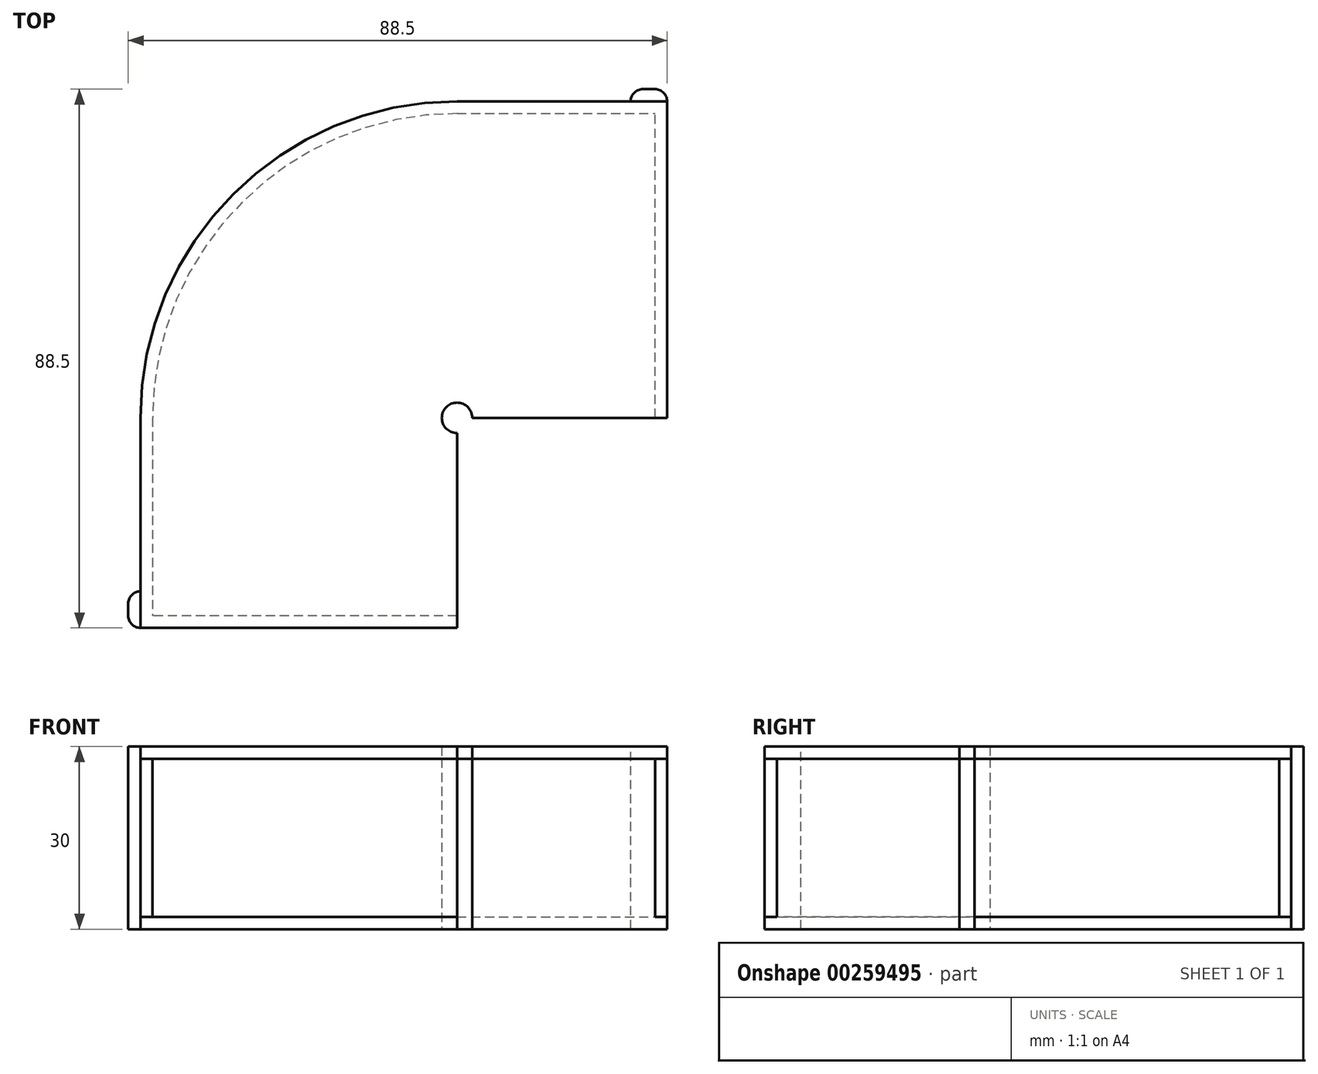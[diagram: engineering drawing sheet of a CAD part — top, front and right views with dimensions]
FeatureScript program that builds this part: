
annotation { "Feature Type Name" : "Feature", "Feature Type Description" : "" }
export const myFeature = defineFeature(function(context is Context, id is Id, definition is map)
    precondition{}
    {
        {
            var Q0;
            Q0=qCreatedBy(makeId("Top.planeOp"),FACE);
            var sketch = newSketch(context, id + "F0", { "sketchPlane" : qUnion([Q0])});
            skLineSegment(sketch, "E0.bottom", {"start": v(2.5, 0) * mm, "end": v(32.5, 0) * mm});
            skLineSegment(sketch, "E0.left", {"start": v(0, -2.5) * mm, "end": v(0, -32.5) * mm});
            skLineSegment(sketch, "E1.0", {"start": v(0, 50) * mm, "end": v(32.5, 50) * mm});
            skLineSegment(sketch, "E1.1", {"start": v(-50, 0) * mm, "end": v(-50, -32.5) * mm});
            skLineSegment(sketch, "E2", {"start": v(0, -32.5) * mm, "end": v(-50, -32.5) * mm});
            skLineSegment(sketch, "E3", {"start": v(32.5, 0) * mm, "end": v(32.5, 50) * mm});
            skArc(sketch, "E4", {"start": v(2.5, 0) * mm, "mid": v(-1.77, 1.77) * mm, "end": v(0, -2.5) * mm});
            skPoint(sketch, "E5.visualSharp", {"position": v(-50, 50) * mm});
            skArc(sketch, "E5.filletArc", {"start": v(0, 50) * mm, "mid": v(-35.36, 35.36) * mm, "end": v(-50, 0) * mm});
            skSolve(sketch);
        }
        {
            var Q0;
            Q0=makeQuery(id+"F0.imprint","IMPRINT",FACE,{"disambiguationData":[TD([[makeQuery(id+"F0.imprint","IMPRINT",EDGE,{"derivedFrom":sQuery(id+"F0.wireOp",EDGE,"E0.bottom")}),1.0]])]});
            extrude(context, id + "F1", {"entities" : qUnion([Q0]), "depth" : 26 * mm});
        }
        {
            var Q0;
            Q0=makeQuery(id+"F1.opExtrude","CAP_FACE",FACE,{"disambiguationData":[OSD([sQuery(id+"F0.wireOp",EDGE,"E0.bottom"),sQuery(id+"F0.wireOp",EDGE,"E0.left"),sQuery(id+"F0.wireOp",EDGE,"E1.0"),sQuery(id+"F0.wireOp",EDGE,"E1.1"),sQuery(id+"F0.wireOp",EDGE,"E2"),sQuery(id+"F0.wireOp",EDGE,"E3"),sQuery(id+"F0.wireOp",EDGE,"E4"),sQuery(id+"F0.wireOp",EDGE,"E5.filletArc")])],"isStart":false});
            var sketch = newSketch(context, id + "F2", { "sketchPlane" : qUnion([Q0])});
            skLineSegment(sketch, "E6.0", {"start": v(34.5, 52) * mm, "end": v(0, 52) * mm});
            skLineSegment(sketch, "E6.1", {"start": v(34.5, 0) * mm, "end": v(34.5, 52) * mm});
            skLineSegment(sketch, "E6.2", {"start": v(-52, 0) * mm, "end": v(-52, -34.5) * mm});
            skLineSegment(sketch, "E6.3", {"start": v(-52, -34.5) * mm, "end": v(0, -34.5) * mm});
            skArc(sketch, "E6.5", {"start": v(0, 52) * mm, "mid": v(-36.77, 36.77) * mm, "end": v(-52, 0) * mm});
            skLineSegment(sketch, "E7.0", {"start": v(2.5, 0) * mm, "end": v(34.5, 0) * mm});
            skArc(sketch, "E8.0", {"start": v(2.5, 0) * mm, "mid": v(-1.77, 1.77) * mm, "end": v(0, -2.5) * mm});
            skLineSegment(sketch, "E9.0", {"start": v(0, -2.5) * mm, "end": v(0, -34.5) * mm});
            skPoint(sketch, "E10.orphan", {"position": v(32.5, 0) * mm});
            skPoint(sketch, "E11.orphan", {"position": v(0, -32.5) * mm});
            skSolve(sketch);
        }
        {
            var Q0;
            Q0=makeQuery(id+"F2.imprint","IMPRINT",FACE,{"disambiguationData":[TD([[makeQuery(id+"F2.imprint","IMPRINT",EDGE,{"derivedFrom":sQuery(id+"F2.wireOp",EDGE,"E6.0")}),1.0]])]});
            var Q1;
            {var subQ1=sQuery(id+"F2.wireOp",EDGE,"E8.0");Q1=makeQuery(id+"F2.imprint","IMPRINT",FACE,{"disambiguationData":[TD([[makeQuery(id+"F2.imprint","IMPRINT",EDGE,{"derivedFrom":subQ1}),-1.0]])]});}
            extrude(context, id + "F3", {"entities" : qUnion([Q0, Q1]), "depth" : 2 * mm});
        }
        {
            var Q0;
            Q0=makeQuery(id+"F1.opExtrude","CAP_FACE",FACE,{"disambiguationData":[OSD([sQuery(id+"F0.wireOp",EDGE,"E0.bottom"),sQuery(id+"F0.wireOp",EDGE,"E0.left"),sQuery(id+"F0.wireOp",EDGE,"E1.0"),sQuery(id+"F0.wireOp",EDGE,"E1.1"),sQuery(id+"F0.wireOp",EDGE,"E2"),sQuery(id+"F0.wireOp",EDGE,"E3"),sQuery(id+"F0.wireOp",EDGE,"E4"),sQuery(id+"F0.wireOp",EDGE,"E5.filletArc")])],"isStart":true});
            var sketch = newSketch(context, id + "F4", { "sketchPlane" : qUnion([Q0])});
            skLineSegment(sketch, "E12.0", {"start": v(-52, 34.5) * mm, "end": v(-52, 0) * mm});
            skLineSegment(sketch, "E12.1", {"start": v(0, 34.5) * mm, "end": v(-52, 34.5) * mm});
            skLineSegment(sketch, "E12.2", {"start": v(0, -52) * mm, "end": v(34.5, -52) * mm});
            skLineSegment(sketch, "E12.3", {"start": v(34.5, -52) * mm, "end": v(34.5, 0) * mm});
            skArc(sketch, "E12.5", {"start": v(-52, 0) * mm, "mid": v(-36.77, -36.77) * mm, "end": v(0, -52) * mm});
            skLineSegment(sketch, "E13.0", {"start": v(2.5, 0) * mm, "end": v(34.5, 0) * mm});
            skArc(sketch, "E14.0", {"start": v(2.5, 0) * mm, "mid": v(-1.77, -1.77) * mm, "end": v(0, 2.5) * mm});
            skLineSegment(sketch, "E14.1", {"start": v(0, 32.5) * mm, "end": v(0, 34.5) * mm});
            skPoint(sketch, "E15.orphan", {"position": v(32.5, 0) * mm});
            skSolve(sketch);
        }
        {
            var Q0;
            Q0=makeQuery(id+"F4.imprint","IMPRINT",FACE,{"disambiguationData":[TD([[makeQuery(id+"F4.imprint","IMPRINT",EDGE,{"derivedFrom":sQuery(id+"F4.wireOp",EDGE,"E12.0")}),1.0]])]});
            var Q1;
            {var subQ0=sQuery(id+"F4.wireOp",EDGE,"E14.0");Q1=makeQuery(id+"F4.imprint","IMPRINT",FACE,{"disambiguationData":[TD([[makeQuery(id+"F4.imprint","IMPRINT",EDGE,{"derivedFrom":subQ0}),1.0]])]});}
            extrude(context, id + "F5", {"entities" : qUnion([Q0, Q1]), "operationType" : NewBodyOperationType.ADD, "depth" : 2 * mm});
        }
        {
            var Q0;
            Q0=makeQuery(id+"F3.opExtrude","CAP_FACE",FACE,{"disambiguationData":[OSD([sQuery(id+"F2.wireOp",EDGE,"E6.0"),sQuery(id+"F2.wireOp",EDGE,"E6.1"),sQuery(id+"F2.wireOp",EDGE,"E6.2"),sQuery(id+"F2.wireOp",EDGE,"E6.3"),sQuery(id+"F2.wireOp",EDGE,"E6.5"),sQuery(id+"F2.wireOp",EDGE,"E7.0"),sQuery(id+"F2.wireOp",EDGE,"E8.0"),sQuery(id+"F2.wireOp",EDGE,"E9.0")])],"isStart":false});
            var sketch = newSketch(context, id + "F6", { "sketchPlane" : qUnion([Q0])});
            skLineSegment(sketch, "E16.bottom", {"start": v(-52, -34.5) * mm, "end": v(-54, -34.5) * mm});
            skLineSegment(sketch, "E16.top", {"start": v(-52, -28.5) * mm, "end": v(-54, -28.5) * mm});
            skLineSegment(sketch, "E16.left", {"start": v(-52, -34.5) * mm, "end": v(-52, -28.5) * mm});
            skLineSegment(sketch, "E16.right", {"start": v(-54, -34.5) * mm, "end": v(-54, -28.5) * mm});
            skLineSegment(sketch, "E17.bottom", {"start": v(34.5, 52) * mm, "end": v(28.5, 52) * mm});
            skLineSegment(sketch, "E17.top", {"start": v(34.5, 54) * mm, "end": v(28.5, 54) * mm});
            skLineSegment(sketch, "E17.left", {"start": v(34.5, 52) * mm, "end": v(34.5, 54) * mm});
            skLineSegment(sketch, "E17.right", {"start": v(28.5, 52) * mm, "end": v(28.5, 54) * mm});
            skSolve(sketch);
        }
        {
            var Q0;
            Q0 = qSketchRegion(id + "F6", true);
            var Q1;
            Q1=makeQuery(id+"F5.opExtrude","CAP_FACE",FACE,{"disambiguationData":[OSD([sQuery(id+"F0.wireOp",EDGE,"E0.left"),sQuery(id+"F4.wireOp",EDGE,"E12.0"),sQuery(id+"F4.wireOp",EDGE,"E12.1"),sQuery(id+"F4.wireOp",EDGE,"E12.2"),sQuery(id+"F4.wireOp",EDGE,"E12.3"),sQuery(id+"F4.wireOp",EDGE,"E12.5"),sQuery(id+"F4.wireOp",EDGE,"E13.0"),sQuery(id+"F4.wireOp",EDGE,"E14.0"),sQuery(id+"F4.wireOp",EDGE,"E14.1")])],"isStart":false});
            extrude(context, id + "F7", {"entities" : qUnion([Q0]), "endBound" : BoundingType.UP_TO_SURFACE, "oppositeDirection" : true, "endBoundEntityFace" : qUnion([Q1]), "depth" : 25 * mm});
        }
        {
            var Q0;
            Q0=makeQuery(id+"F7.opExtrude","SWEPT_EDGE",EDGE,{"disambiguationData":[OSD([sQuery(id+"F6.wireOp",EDGE,"E17.top"),sQuery(id+"F6.wireOp",EDGE,"E17.right")])]});
            var Q1;
            Q1=makeQuery(id+"F7.opExtrude","SWEPT_EDGE",EDGE,{"disambiguationData":[OSD([sQuery(id+"F6.wireOp",EDGE,"E16.top"),sQuery(id+"F6.wireOp",EDGE,"E16.right")])]});
            var Q2;
            Q2=makeQuery(id+"F7.opExtrude","SWEPT_EDGE",EDGE,{"disambiguationData":[OSD([sQuery(id+"F6.wireOp",EDGE,"E16.bottom"),sQuery(id+"F6.wireOp",EDGE,"E16.right")])]});
            var Q3;
            Q3=makeQuery(id+"F7.opExtrude","SWEPT_EDGE",EDGE,{"disambiguationData":[OSD([sQuery(id+"F6.wireOp",EDGE,"E17.top"),sQuery(id+"F6.wireOp",EDGE,"E17.left")])]});
            fillet(context, id + "F8", {"entities" : qUnion([Q0, Q1, Q2, Q3]), "radius" : 2 * mm, "tangentPropagation" : true, "allowEdgeOverflow" : false});
        }
    });
